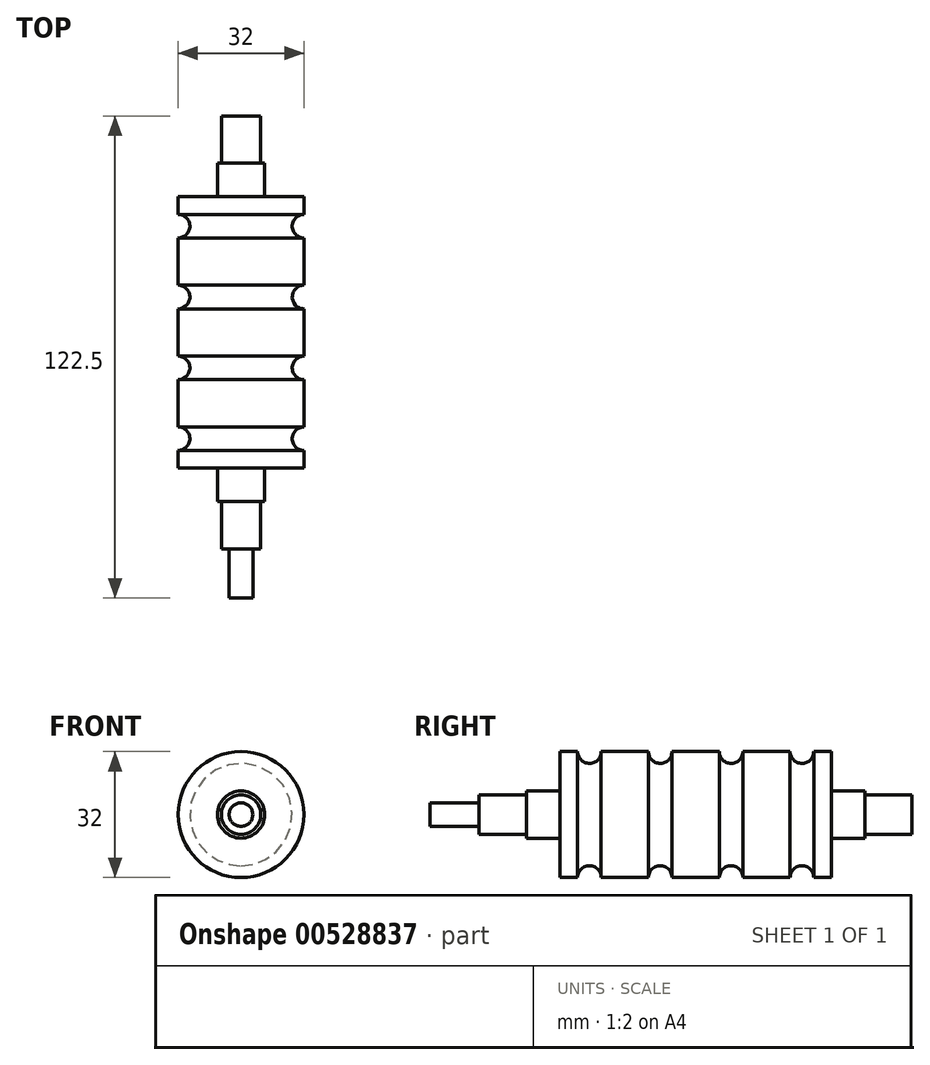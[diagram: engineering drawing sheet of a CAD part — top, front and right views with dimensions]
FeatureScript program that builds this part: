
annotation { "Feature Type Name" : "Feature", "Feature Type Description" : "" }
export const myFeature = defineFeature(function(context is Context, id is Id, definition is map)
    precondition{}
    {
        {
            var Q0;
            Q0=qCreatedBy(makeId("Front.planeOp"),FACE);
            var sketch = newSketch(context, id + "F0", { "sketchPlane" : qUnion([Q0])});
            skCircle(sketch, "E0", {"center": v(0, 0) * mm, "radius": 16 * mm});
            skSolve(sketch);
        }
        {
            var Q0;
            Q0=qSketchRegion(id+"F0",true);
            extrude(context, id + "F1", {"entities" : qUnion([Q0]), "endBound" : BoundingType.SYMMETRIC, "depth" : 69 * mm, "offsetDistance" : 25 * mm});
        }
        {
            var Q0;
            Q0=qCreatedBy(makeId("Right.planeOp"),FACE);
            var sketch = newSketch(context, id + "F2", { "sketchPlane" : qUnion([Q0])});
            skCircle(sketch, "E1.1.0.0", {"center": v(9, 16) * mm, "radius": 3 * mm});
            skCircle(sketch, "E1.3.0.0", {"center": v(27, 16) * mm, "radius": 3 * mm});
            skLineSegment(sketch, "E1.direction1", {"start": v(0, 16) * mm, "end": v(9, 16) * mm, "construction": true});
            skCircle(sketch, "E2.1.0.0", {"center": v(-9, 16) * mm, "radius": 3 * mm});
            skCircle(sketch, "E2.3.0.0", {"center": v(-27, 16) * mm, "radius": 3 * mm});
            skLineSegment(sketch, "E2.direction1", {"start": v(0, 16) * mm, "end": v(-9, 16) * mm, "construction": true});
            skSolve(sketch);
        }
        {
            var Q0;
            Q0=makeQuery(id+"F2.imprint","IMPRINT",FACE,{"disambiguationData":[TD([[makeQuery(id+"F2.imprint","IMPRINT",EDGE,{"derivedFrom":sQuery(id+"F2.wireOp",EDGE,"E2.3.0.0")}),1.0]])]});
            var Q1;
            Q1=makeQuery(id+"F2.imprint","IMPRINT",FACE,{"disambiguationData":[TD([[makeQuery(id+"F2.imprint","IMPRINT",EDGE,{"derivedFrom":sQuery(id+"F2.wireOp",EDGE,"E2.2.0.0")}),1.0]])]});
            var Q2;
            Q2=makeQuery(id+"F2.imprint","IMPRINT",FACE,{"disambiguationData":[TD([[makeQuery(id+"F2.imprint","IMPRINT",EDGE,{"derivedFrom":sQuery(id+"F2.wireOp",EDGE,"E2.1.0.0")}),1.0]])]});
            var Q3;
            Q3=makeQuery(id+"F2.imprint","IMPRINT",FACE,{"disambiguationData":[TD([[makeQuery(id+"F2.imprint","IMPRINT",EDGE,{"derivedFrom":sQuery(id+"F2.wireOp",EDGE,"Xp1CqcSZ-3eiH-poQm-56Av-rw8gismURRpS")}),1.0]])]});
            var Q4;
            Q4=makeQuery(id+"F2.imprint","IMPRINT",FACE,{"disambiguationData":[TD([[makeQuery(id+"F2.imprint","IMPRINT",EDGE,{"derivedFrom":sQuery(id+"F2.wireOp",EDGE,"E1.1.0.0")}),1.0]])]});
            var Q5;
            Q5=makeQuery(id+"F2.imprint","IMPRINT",FACE,{"disambiguationData":[TD([[makeQuery(id+"F2.imprint","IMPRINT",EDGE,{"derivedFrom":sQuery(id+"F2.wireOp",EDGE,"E1.2.0.0")}),1.0]])]});
            var Q6;
            Q6=makeQuery(id+"F2.imprint","IMPRINT",FACE,{"disambiguationData":[TD([[makeQuery(id+"F2.imprint","IMPRINT",EDGE,{"derivedFrom":sQuery(id+"F2.wireOp",EDGE,"E1.3.0.0")}),1.0]])]});
            var Q7;
            Q7=makeQuery(id+"F1.opExtrude","CAP_EDGE",EDGE,{"disambiguationData":[OSD([sQuery(id+"F0.wireOp",EDGE,"E0")])],"isStart":false});
            revolve(context, id + "F3", {"operationType" : NewBodyOperationType.REMOVE, "entities" : qUnion([Q0, Q1, Q2, Q3, Q4, Q5, Q6]), "axis" : qUnion([Q7]), "revolveType" : RevolveType.FULL, "oppositeDirection" : true});
        }
        {
            var Q0;
            Q0=qCreatedBy(makeId("Front.planeOp"),FACE);
            var sketch = newSketch(context, id + "F4", { "sketchPlane" : qUnion([Q0])});
            skCircle(sketch, "E3", {"center": v(0, 0) * mm, "radius": 6 * mm});
            skSolve(sketch);
        }
        {
            var Q0;
            Q0 = qSketchRegion(id + "F4", true);
            extrude(context, id + "F5", {"entities" : qUnion([Q0]), "operationType" : NewBodyOperationType.ADD, "depth" : 43 * mm, "offsetDistance" : 25 * mm, "hasSecondDirection" : true, "secondDirectionOppositeDirection" : true, "secondDirectionDepth" : 43 * mm});
        }
        {
            var Q0;
            Q0=qCreatedBy(makeId("Front.planeOp"),FACE);
            var sketch = newSketch(context, id + "F6", { "sketchPlane" : qUnion([Q0])});
            skCircle(sketch, "E4", {"center": v(0, 0) * mm, "radius": 5 * mm});
            skSolve(sketch);
        }
        {
            var Q0;
            Q0 = qSketchRegion(id + "F6", true);
            extrude(context, id + "F7", {"entities" : qUnion([Q0]), "operationType" : NewBodyOperationType.ADD, "depth" : 55 * mm, "offsetDistance" : 25 * mm, "hasSecondDirection" : true, "secondDirectionOppositeDirection" : true, "secondDirectionDepth" : 55 * mm});
        }
        {
            var Q0;
            Q0=makeQuery(id+"F7.opExtrude","CAP_FACE",FACE,{"disambiguationData":[OSD([sQuery(id+"F6.wireOp",EDGE,"E4")])],"isStart":false});
            var sketch = newSketch(context, id + "F8", { "sketchPlane" : qUnion([Q0])});
            skCircle(sketch, "E5", {"center": v(0, 0) * mm, "radius": 3 * mm});
            skSolve(sketch);
        }
        {
            var Q0;
            Q0=makeQuery(id+"F8.imprint","IMPRINT",FACE,{"disambiguationData":[TD([[makeQuery(id+"F8.imprint","IMPRINT",EDGE,{"derivedFrom":sQuery(id+"F8.wireOp",EDGE,"E5")}),1.0]])]});
            var Q1;
            Q1=sQuery(id+"F8.wireOp",EDGE,"E5");
            extrude(context, id + "F9", {"entities" : qUnion([Q0]), "operationType" : NewBodyOperationType.ADD, "surfaceEntities" : qUnion([Q1]), "depth" : 12.5 * mm, "offsetDistance" : 25 * mm});
        }
    });
